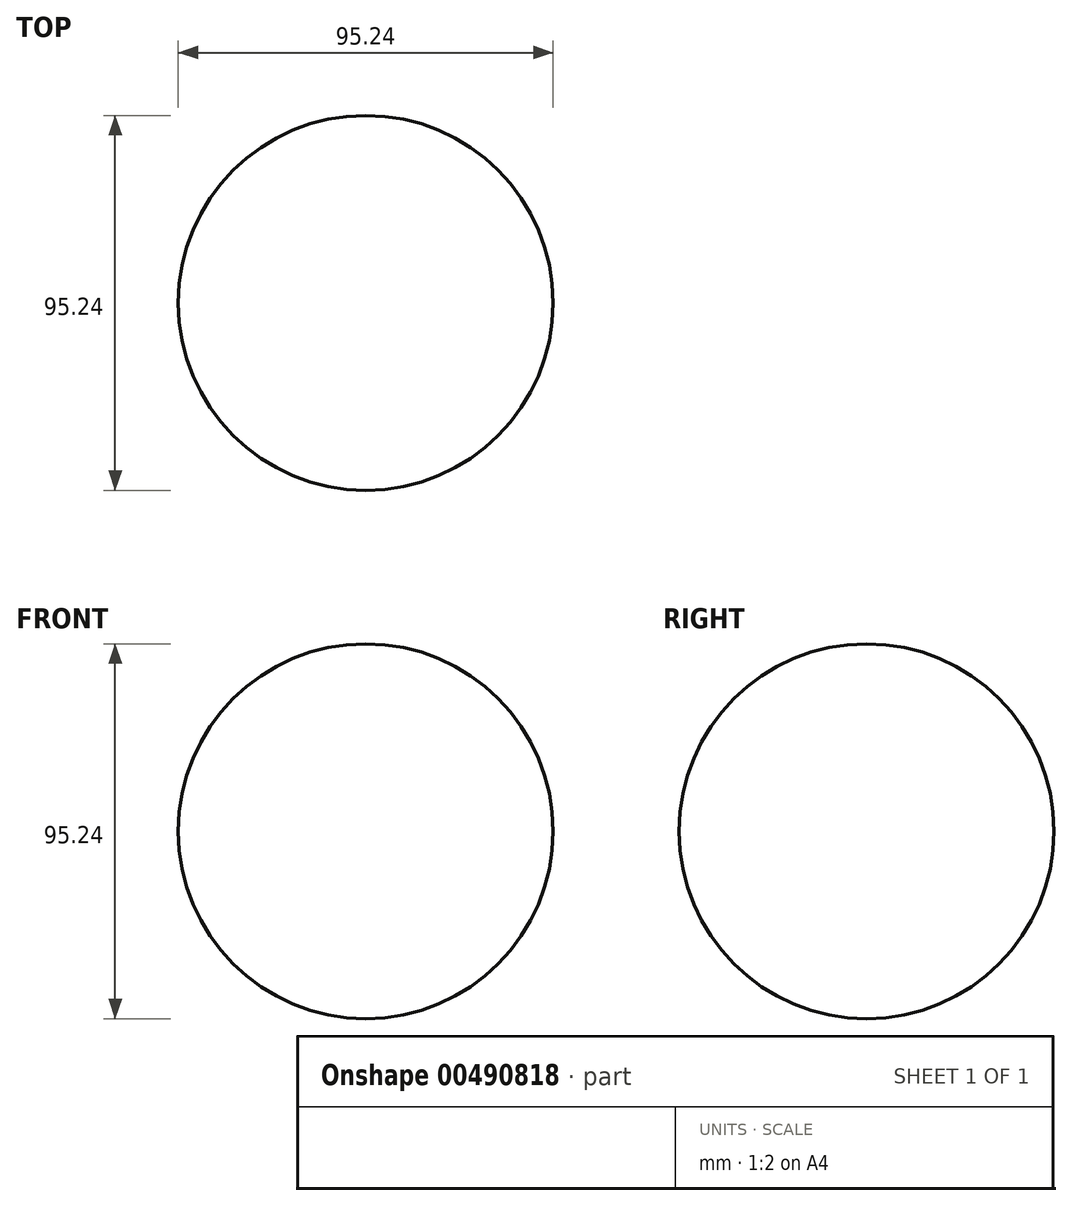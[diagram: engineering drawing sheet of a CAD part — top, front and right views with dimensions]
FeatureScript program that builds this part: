
annotation { "Feature Type Name" : "Feature", "Feature Type Description" : "" }
export const myFeature = defineFeature(function(context is Context, id is Id, definition is map)
    precondition{}
    {
        {
            var Q0;
            Q0=qCreatedBy(makeId("Front.planeOp"),FACE);
            var sketch = newSketch(context, id + "F0", { "sketchPlane" : qUnion([Q0])});
            skArc(sketch, "E0", {"start": v(0, -47.63) * mm, "mid": v(47.63, 0) * mm, "end": v(0, 47.63) * mm});
            skLineSegment(sketch, "E1", {"start": v(0, -47.63) * mm, "end": v(0, 47.63) * mm});
            skSolve(sketch);
        }
        {
            var Q0;
            Q0 = qSketchRegion(id + "F0", true);
            var Q1;
            Q1=sQuery(id+"F0.wireOp",EDGE,"E1");
            revolve(context, id + "F1", {"entities" : qUnion([Q0]), "axis" : qUnion([Q1]), "revolveType" : RevolveType.FULL});
        }
    });
